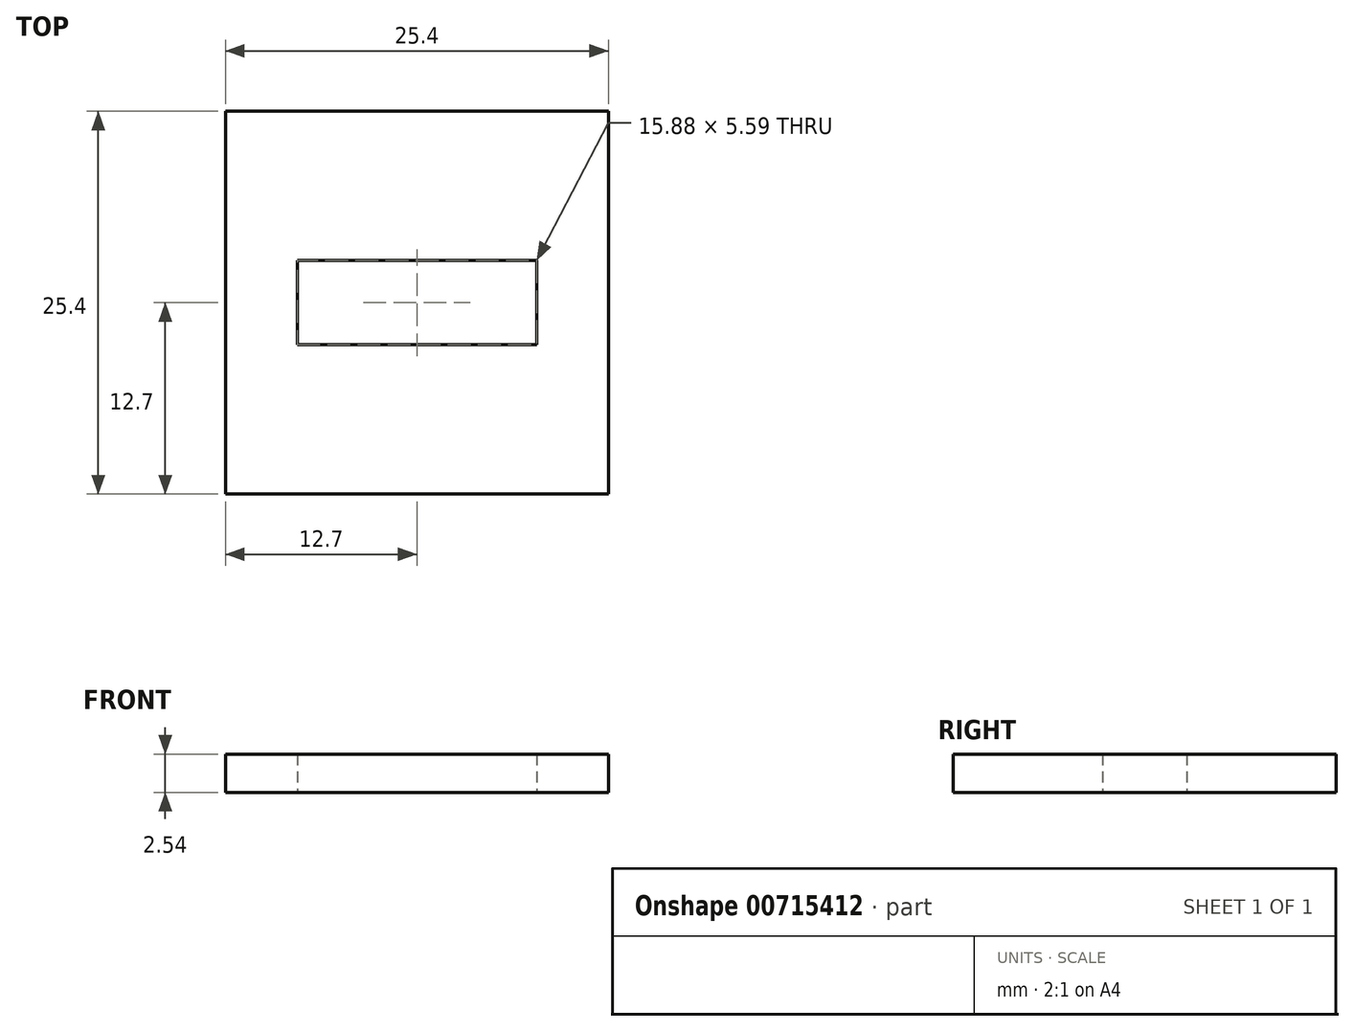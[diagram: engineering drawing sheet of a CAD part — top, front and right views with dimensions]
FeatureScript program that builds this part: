
annotation { "Feature Type Name" : "Feature", "Feature Type Description" : "" }
export const myFeature = defineFeature(function(context is Context, id is Id, definition is map)
    precondition{}
    {
        {
            var Q0;
            Q0=qCreatedBy(makeId("Top.planeOp"),FACE);
            var sketch = newSketch(context, id + "F0", { "sketchPlane" : qUnion([Q0])});
            skLineSegment(sketch, "E0.bottom", {"start": v(0, 0) * mm, "end": v(25.4, 0) * mm});
            skLineSegment(sketch, "E0.top", {"start": v(0, 25.4) * mm, "end": v(25.4, 25.4) * mm});
            skLineSegment(sketch, "E0.left", {"start": v(0, 0) * mm, "end": v(0, 25.4) * mm});
            skLineSegment(sketch, "E0.right", {"start": v(25.4, 0) * mm, "end": v(25.4, 25.4) * mm});
            skPoint(sketch, "E1.endSnap0", {"position": v(25.4, 12.7) * mm});
            skPoint(sketch, "E2.start.orphan", {"position": v(12.7, 12.7) * mm});
            skLineSegment(sketch, "E3.bottom", {"start": v(20.64, 15.5) * mm, "end": v(4.76, 15.5) * mm});
            skLineSegment(sketch, "E3.top", {"start": v(20.64, 9.9) * mm, "end": v(4.76, 9.9) * mm});
            skLineSegment(sketch, "E3.left", {"start": v(20.64, 15.5) * mm, "end": v(20.64, 9.9) * mm});
            skLineSegment(sketch, "E3.right", {"start": v(4.76, 15.5) * mm, "end": v(4.76, 9.9) * mm});
            skSolve(sketch);
        }
        {
            var Q0;
            Q0=makeQuery(id+"F0.imprint","IMPRINT",FACE,{"disambiguationData":[TD([[makeQuery(id+"F0.imprint","IMPRINT",EDGE,{"derivedFrom":sQuery(id+"F0.wireOp",EDGE,"E0.bottom")}),1.0]])]});
            extrude(context, id + "F1", {"entities" : qUnion([Q0]), "depth" : 2.54 * mm, "offsetDistance" : 25.4 * mm});
        }
    });
